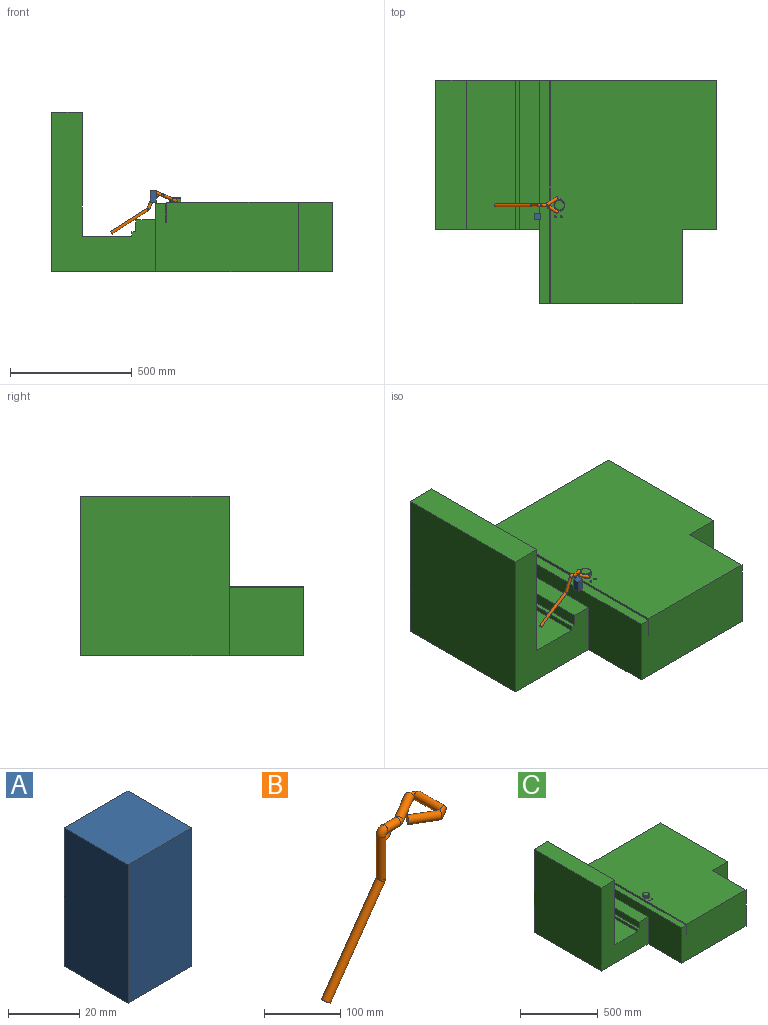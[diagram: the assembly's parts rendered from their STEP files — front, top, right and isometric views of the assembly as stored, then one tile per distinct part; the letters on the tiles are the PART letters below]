
ASSEMBLY  parts=3 mates=2
PART A: 6 faces, bbox 25.4x25.4x47.6 mm
  f0: plane 47.63x25.4mm, normal (-1,0,0), area 1209.7mm2, adj f1,f3,f4,f5
  f1: plane 47.63x25.4mm, normal (0,-1,0), area 1209.7mm2, adj f0,f2,f4,f5
  f2: plane 47.63x25.4mm, normal (1,0,0), area 1209.7mm2, adj f1,f3,f4,f5
  f3: plane 47.63x25.4mm, normal (0,1,0), area 1209.7mm2, adj f0,f2,f4,f5
  f4: plane 25.4x25.4mm, normal (0,0,1), area 645.2mm2, adj f0,f1,f2,f3
  f5: plane 25.4x25.4mm, normal (0,0,-1), area 645.2mm2, adj f0,f1,f2,f3
PART B: 13 faces, bbox 205.3x75.1x232.9 mm
  f0: plane 12.7x10.4mm, normal (-0.57,0,-0.82), area 126.7mm2, adj f2
  f1: plane 12.7x10.93mm, normal (-0.86,0.51,0), area 126.7mm2, adj f12
  f2: cylinder r=6.35mm len=151.29mm, axis (0.57,0,0.82), area 7014mm2, adj f0,f3
  f3: torus R=6.35mm, axis (0,-1,0), area 154.8mm2, adj f2,f4
  f4: cylinder r=6.35mm len=67.85mm, axis (0,0,1), area 2707mm2, adj f3,f5
  f5: torus R=6.35mm, axis (0,1,0), area 398mm2, adj f4,f6
  f6: cylinder r=6.35mm len=23.56mm, axis (1,0,0), area 940mm2, adj f5,f7
  f7: torus R=6.35mm, axis (0,0,1), area 135.2mm2, adj f6,f8
  f8: cylinder r=6.35mm len=54.49mm, axis (0.86,0.51,0), area 2226mm2, adj f7,f9
  f9: torus R=6.35mm, axis (0,0,-1), area 533.2mm2, adj f8,f10
  f10: cylinder r=6.35mm len=47.59mm, axis (0,-1,0), area 1898.9mm2, adj f9,f11
  f11: torus R=6.35mm, axis (0,0,-1), area 533.2mm2, adj f10,f12
  f12: cylinder r=6.35mm len=45.05mm, axis (-0.86,0.51,0), area 1788.5mm2, adj f1,f11
PART C: 29 faces, bbox 1151.7x914.4x652.7 mm
  f0: plane 652.69x426.76mm, normal (0,-1,0), area 131604.7mm2, adj f1,f2,f3,f4,f5,f12,f13,f14
  f1: plane 609.6x203.2mm, normal (0,0,1), area 123870.7mm2, adj f0,f2,f16,f18
  f2: plane 609.6x507.56mm, normal (1,0,0), area 309409.5mm2, adj f0,f1,f3,f18
  f3: plane 609.6x125.93mm, normal (0,0,1), area 76764.1mm2, adj f0,f2,f4,f18
  f4: plane 652.69x609.6mm, normal (-1,0,0), area 397882.3mm2, adj f0,f3,f5,f18
  f5: plane 1151.7x914.4mm, normal (0,0,-1), area 880463.7mm2, adj f0,f4,f6,f12,f17,f18,f26,f27
  f6: plane 609.6x284.83mm, normal (1,0,0), area 173634mm2, adj f5,f7,f17,f18
  f7: plane 914.4x680.5mm, normal (0,0,1), area 577996.3mm2, adj f6,f8,f17,f18,f19,f21,f23,f26
  f8: plane 914.4x82.55mm, normal (-1,0,0), area 75483.7mm2, adj f7,f9,f18,f27
  f9: plane 914.4x3.18mm, normal (0,0,1), area 2903.2mm2, adj f8,f10,f18,f27
  f10: plane 914.4x76.2mm, normal (1,0,0), area 69677.3mm2, adj f9,f11,f18,f27
  f11: plane 914.4x41.28mm, normal (0,0,1), area 37741.9mm2, adj f10,f12,f18,f27
  f12: plane 914.4x278.48mm, normal (-1,0,0), area 125526.6mm2, adj f0,f5,f11,f13,f18,f27
  f13: plane 609.6x81.76mm, normal (0,0,1), area 49838.6mm2, adj f0,f12,f14,f18
  f14: plane 609.6x47.63mm, normal (-1,0,0), area 29032.2mm2, adj f0,f13,f15,f18
  f15: plane 609.6x15.88mm, normal (0,0,1), area 9677.4mm2, adj f0,f14,f16,f18
  f16: plane 609.6x19.05mm, normal (-1,0,0), area 11612.9mm2, adj f0,f1,f15,f18
  f17: plane 284.83x139.7mm, normal (0,-1,0), area 39790.3mm2, adj f5,f6,f7,f26
  f18: plane 1151.7x652.69mm, normal (0,1,0), area 337569.4mm2, adj f1,f2,f3,f4,f5,f6,f7,f8
  f19: cylinder r=4.37mm len=50.8mm, axis (0,0,1), area 1393.4mm2, adj f7,f20
  f20: plane 8.73x8.73mm, normal (0,0,1), area 59.9mm2, adj f19
  f21: cylinder r=4.37mm len=50.8mm, axis (0,0,1), area 1393.4mm2, adj f7,f22
  f22: plane 8.73x8.73mm, normal (0,0,1), area 59.9mm2, adj f21
  f23: cylinder r=22.23mm len=44.45mm, axis (0,0,-1), area 2049.2mm2, adj f7,f25,f28
  f24: plane 39.37x39.37mm, normal (0,0,1), area 1217.4mm2, adj f25
  f25: torus R=19.69mm, axis (0,0,1), area 534mm2, adj f23,f24
  f26: plane 304.8x284.83mm, normal (1,0,0), area 86817mm2, adj f5,f7,f17,f27
  f27: plane 585.25x284.83mm, normal (0,-1,0), area 166174.4mm2, adj f5,f7,f8,f9,f10,f11,f12,f26
  f28: cylinder r=6.35mm len=44.45mm, axis (0,-1,0), area 1736mm2, adj f23
PLACE A t=(55.72,-104.87,27.64)mm
PLACE B rot(axis=(0,1,0),22.2deg) t=(-248.21,813.37,43.12)mm
PLACE C t=(-221.93,466.63,-112.06)mm fixed
MATE cylindrical B.f10 <-> C.f28  axis (0,-1,0) through (160.46,-44.48,33.99)mm
MATE planar A.f5 <-> C.f21  axis (0,0,-1) through (68.42,-92.17,27.64)mm
